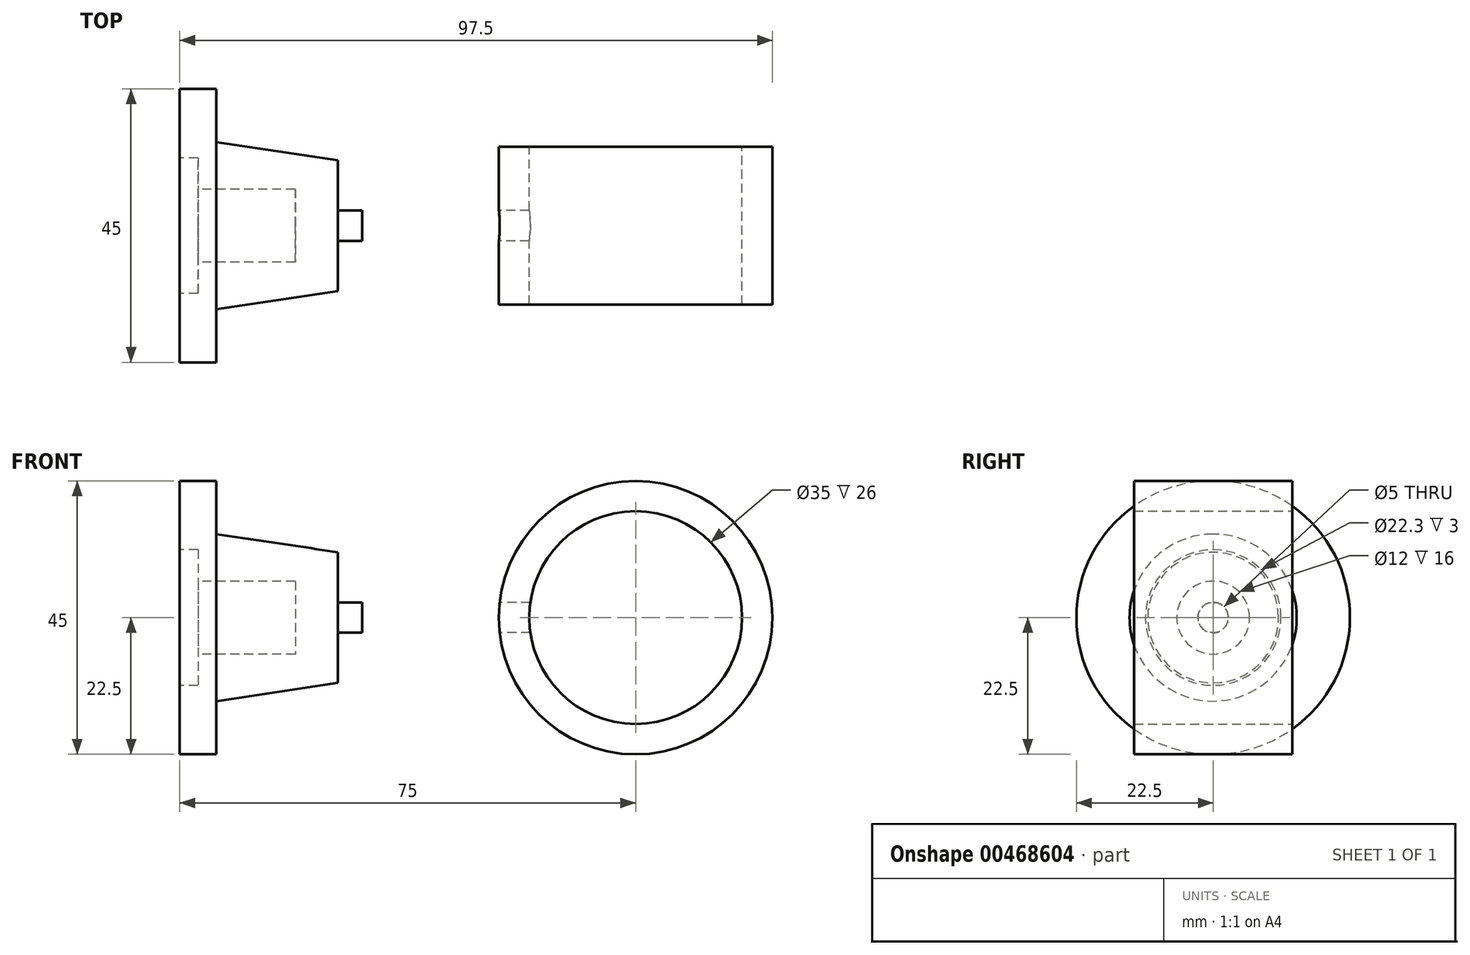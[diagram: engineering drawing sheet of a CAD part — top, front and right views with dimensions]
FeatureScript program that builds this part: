
annotation { "Feature Type Name" : "Feature", "Feature Type Description" : "" }
export const myFeature = defineFeature(function(context is Context, id is Id, definition is map)
    precondition{}
    {
        {
            var Q0;
            Q0=qCreatedBy(makeId("Front.planeOp"),FACE);
            var sketch = newSketch(context, id + "F0", { "sketchPlane" : qUnion([Q0])});
            skLineSegment(sketch, "E0", {"start": v(0, 0) * mm, "end": v(0, 22.5) * mm});
            skLineSegment(sketch, "E1", {"start": v(0, 22.5) * mm, "end": v(6, 22.5) * mm});
            skLineSegment(sketch, "E2", {"start": v(6, 22.5) * mm, "end": v(6, 0) * mm});
            skLineSegment(sketch, "E3", {"start": v(6, 0) * mm, "end": v(0, 0) * mm});
            skPoint(sketch, "E4", {"position": v(6, 13.75) * mm});
            skLineSegment(sketch, "E5", {"start": v(6, 0) * mm, "end": v(26, 0) * mm});
            skLineSegment(sketch, "E6", {"start": v(26, 0) * mm, "end": v(26, 10.75) * mm});
            skLineSegment(sketch, "E7", {"start": v(26, 10.75) * mm, "end": v(6, 13.75) * mm});
            skPoint(sketch, "E8", {"position": v(26, 2.5) * mm});
            skLineSegment(sketch, "E9", {"start": v(26, 2.5) * mm, "end": v(30, 2.5) * mm});
            skLineSegment(sketch, "E10", {"start": v(30, 2.5) * mm, "end": v(30, 0) * mm});
            skLineSegment(sketch, "E11", {"start": v(30, 0) * mm, "end": v(26, 0) * mm});
            skPoint(sketch, "E12", {"position": v(0, 11.15) * mm});
            skLineSegment(sketch, "E13", {"start": v(0, 11.15) * mm, "end": v(3, 11.15) * mm});
            skLineSegment(sketch, "E14", {"start": v(3, 11.15) * mm, "end": v(3, 0) * mm});
            skPoint(sketch, "E15", {"position": v(3, 6) * mm});
            skLineSegment(sketch, "E16", {"start": v(3, 6) * mm, "end": v(19, 6) * mm});
            skLineSegment(sketch, "E17", {"start": v(19, 6) * mm, "end": v(19, 0) * mm});
            skSolve(sketch);
        }
        {
            var Q0;
            {var subQ4=sQuery(id+"F0.wireOp",EDGE,"E1");Q0=makeQuery(id+"F0.imprint","IMPRINT",FACE,{"disambiguationData":[TD([[makeQuery(id+"F0.imprint","IMPRINT",EDGE,{"derivedFrom":subQ4}),-1.0]])]});}
            var Q1;
            {var subQ0=sQuery(id+"F0.wireOp",EDGE,"E7");Q1=makeQuery(id+"F0.imprint","IMPRINT",FACE,{"disambiguationData":[TD([[makeQuery(id+"F0.imprint","IMPRINT",EDGE,{"derivedFrom":subQ0}),1.0]])]});}
            var Q2;
            {var subQ2=sQuery(id+"F0.wireOp",EDGE,"E9");Q2=makeQuery(id+"F0.imprint","IMPRINT",FACE,{"disambiguationData":[TD([[makeQuery(id+"F0.imprint","IMPRINT",EDGE,{"derivedFrom":subQ2}),-1.0]])]});}
            var Q3;
            Q3=sQuery(id+"F0.wireOp",EDGE,"E5");
            revolve(context, id + "F1", {"entities" : qUnion([Q0, Q1, Q2]), "axis" : qUnion([Q3]), "revolveType" : RevolveType.FULL});
        }
        {
            var Q0;
            Q0=qCreatedBy(makeId("Front.planeOp"),FACE);
            var sketch = newSketch(context, id + "F2", { "sketchPlane" : qUnion([Q0])});
            skLineSegment(sketch, "E18", {"start": v(0, 0) * mm, "end": v(75, 0) * mm});
            skCircle(sketch, "E19", {"center": v(75, 0) * mm, "radius": 22.5 * mm});
            skCircle(sketch, "E20", {"center": v(75, 0) * mm, "radius": 17.5 * mm});
            skSolve(sketch);
        }
        {
            var Q0;
            Q0=qSketchRegion(id+"F2",true);
            extrude(context, id + "F3", {"entities" : qUnion([Q0]), "depth" : 26 * mm, "symmetric" : true});
        }
        {
            var Q0;
            Q0=qCreatedBy(makeId("Right.planeOp"),FACE);
            cPlane(context, id + "F4", {"entities" : qUnion([Q0]), "cplaneType" : CPlaneType.OFFSET, "offset" : 56 * mm, "width" : 150 * mm, "height" : 150 * mm});
        }
        {
            var Q0;
            Q0=qCreatedBy(id+"F4.planeOp",FACE);
            var sketch = newSketch(context, id + "F5", { "sketchPlane" : qUnion([Q0])});
            skCircle(sketch, "E21", {"center": v(0, 0) * mm, "radius": 2.5 * mm});
            skSolve(sketch);
        }
        {
            var Q0;
            Q0=qSketchRegion(id+"F5",true);
            extrude(context, id + "F6", {"entities" : qUnion([Q0]), "operationType" : NewBodyOperationType.REMOVE, "depth" : 10 * mm, "symmetric" : true});
        }
    });
